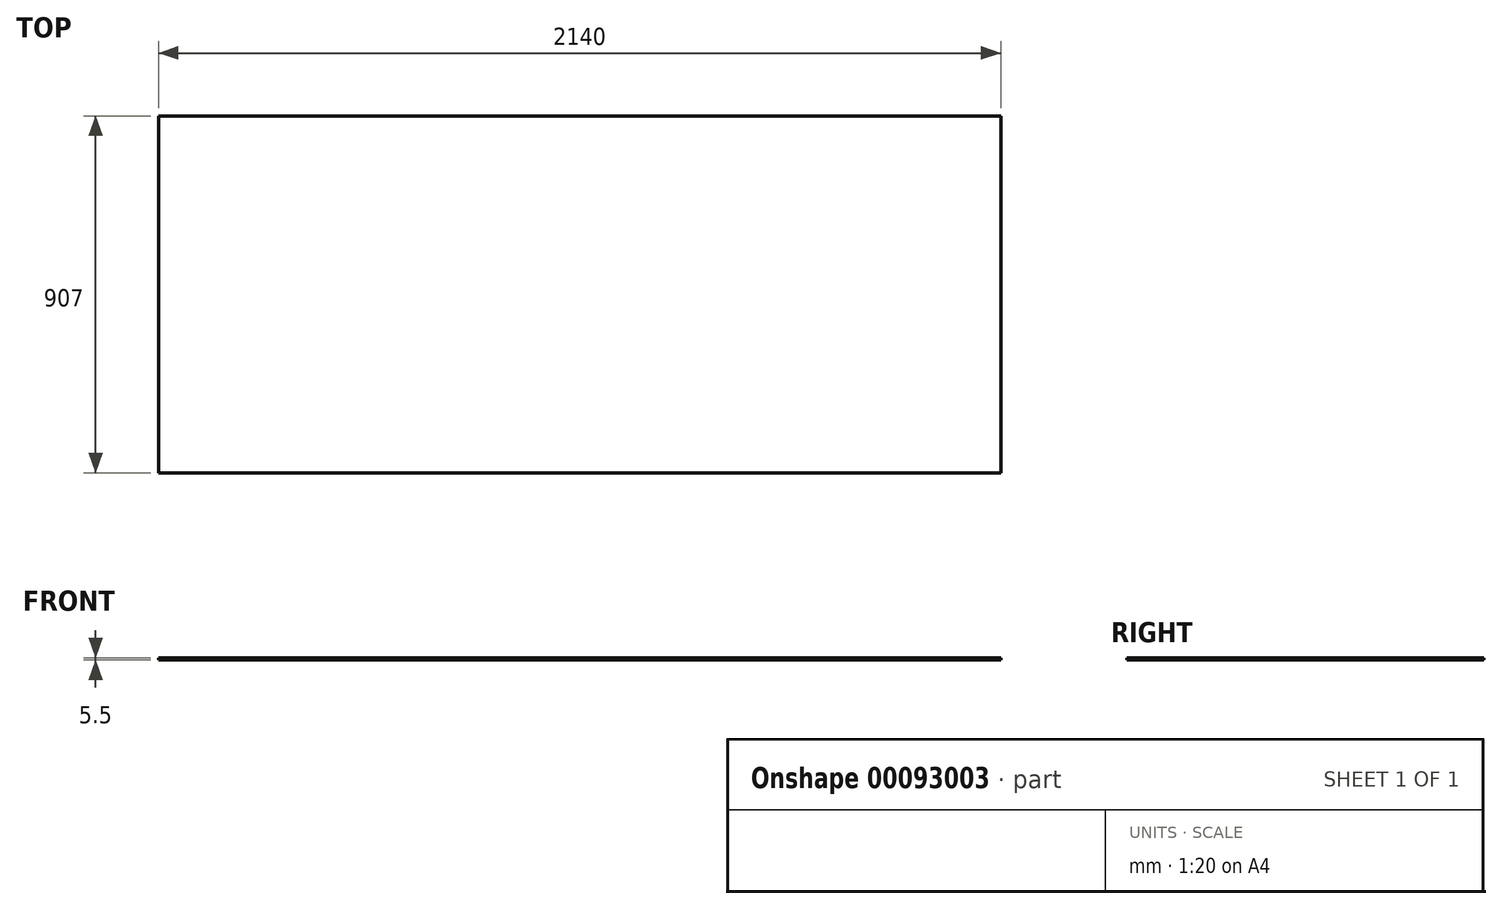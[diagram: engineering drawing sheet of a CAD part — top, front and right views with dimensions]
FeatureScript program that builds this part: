
annotation { "Feature Type Name" : "Feature", "Feature Type Description" : "" }
export const myFeature = defineFeature(function(context is Context, id is Id, definition is map)
    precondition{}
    {
        {
            var Q0;
            Q0=qCreatedBy(makeId("Top.planeOp"),FACE);
            var sketch = newSketch(context, id + "F0", { "sketchPlane" : qUnion([Q0])});
            skLineSegment(sketch, "E0.bottom", {"start": v(0, 0) * mm, "end": v(2140, 0) * mm});
            skLineSegment(sketch, "E0.top", {"start": v(0, 907) * mm, "end": v(2140, 907) * mm});
            skLineSegment(sketch, "E0.left", {"start": v(0, 0) * mm, "end": v(0, 907) * mm});
            skLineSegment(sketch, "E0.right", {"start": v(2140, 0) * mm, "end": v(2140, 907) * mm});
            skSolve(sketch);
        }
        {
            var Q0;
            Q0=makeQuery(id+"F0.imprint","IMPRINT",FACE,{"disambiguationData":[TD([[makeQuery(id+"F0.imprint","IMPRINT",EDGE,{"derivedFrom":sQuery(id+"F0.wireOp",EDGE,"E0.bottom")}),1.0]])]});
            extrude(context, id + "F1", {"entities" : qUnion([Q0]), "depth" : 5.5 * mm});
        }
    });
